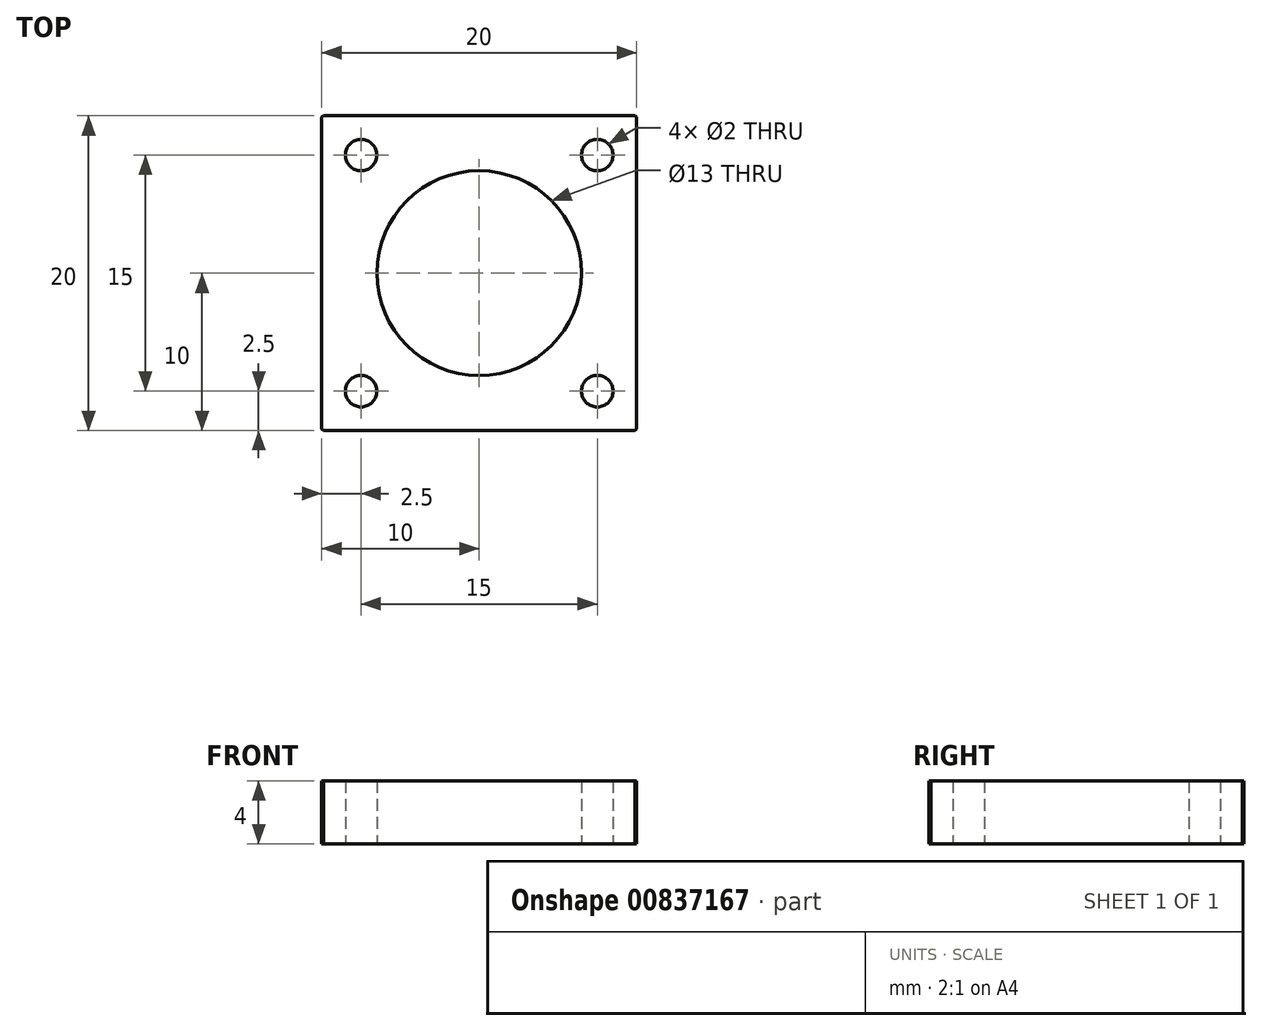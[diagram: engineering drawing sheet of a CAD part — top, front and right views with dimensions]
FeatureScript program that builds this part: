
annotation { "Feature Type Name" : "Feature", "Feature Type Description" : "" }
export const myFeature = defineFeature(function(context is Context, id is Id, definition is map)
    precondition{}
    {
        {
            var Q0;
            Q0=qCreatedBy(makeId("Top.planeOp"),FACE);
            var sketch = newSketch(context, id + "F0", { "sketchPlane" : qUnion([Q0])});
            skLineSegment(sketch, "E0.bottom", {"start": v(0, 0) * mm, "end": v(20, 0) * mm});
            skLineSegment(sketch, "E0.top", {"start": v(0, -20) * mm, "end": v(20, -20) * mm});
            skLineSegment(sketch, "E0.left", {"start": v(0, 0) * mm, "end": v(0, -20) * mm});
            skLineSegment(sketch, "E0.right", {"start": v(20, 0) * mm, "end": v(20, -20) * mm});
            skLineSegment(sketch, "E1", {"start": v(0, -10) * mm, "end": v(20, -10) * mm, "construction": true});
            skCircle(sketch, "E2", {"center": v(10, -10) * mm, "radius": 2 * mm});
            skCircle(sketch, "E3", {"center": v(10, -10) * mm, "radius": 5.5 * mm, "construction": true});
            skCircle(sketch, "E4", {"center": v(10, -10) * mm, "radius": 6.5 * mm});
            skCircle(sketch, "E5", {"center": v(10, -10) * mm, "radius": 7 * mm});
            skCircle(sketch, "E6", {"center": v(10, -10) * mm, "radius": 8.5 * mm});
            skCircle(sketch, "E7", {"center": v(10, -10) * mm, "radius": 3 * mm});
            skLineSegment(sketch, "E8", {"start": v(10, -10) * mm, "end": v(10, -5.75) * mm, "construction": true});
            skCircle(sketch, "E9", {"center": v(10, -5.75) * mm, "radius": 1.25 * mm});
            skCircle(sketch, "E10.1.0", {"center": v(5.75, -10) * mm, "radius": 1.25 * mm});
            skCircle(sketch, "E10.2.0", {"center": v(10, -14.25) * mm, "radius": 1.25 * mm});
            skCircle(sketch, "E10.3.0", {"center": v(14.25, -10) * mm, "radius": 1.25 * mm});
            skLineSegment(sketch, "E11", {"start": v(0, -2.5) * mm, "end": v(2.5, -2.5) * mm, "construction": true});
            skLineSegment(sketch, "E12", {"start": v(2.5, -2.5) * mm, "end": v(2.5, 0) * mm, "construction": true});
            skCircle(sketch, "E13", {"center": v(2.5, -2.5) * mm, "radius": 1 * mm});
            skCircle(sketch, "E14.1.0", {"center": v(2.5, -17.5) * mm, "radius": 1 * mm});
            skCircle(sketch, "E14.2.0", {"center": v(17.5, -17.5) * mm, "radius": 1 * mm});
            skCircle(sketch, "E14.3.0", {"center": v(17.5, -2.5) * mm, "radius": 1 * mm});
            skSolve(sketch);
        }
        {
            var Q0;
            Q0=makeQuery(id+"F0.imprint","IMPRINT",FACE,{"disambiguationData":[TD([[makeQuery(id+"F0.imprint","IMPRINT",EDGE,{"derivedFrom":sQuery(id+"F0.wireOp",EDGE,"E0.bottom")}),-1.0]])]});
            var Q1;
            Q1=makeQuery(id+"F0.imprint","IMPRINT",FACE,{"disambiguationData":[TD([[makeQuery(id+"F0.imprint","IMPRINT",EDGE,{"derivedFrom":sQuery(id+"F0.wireOp",EDGE,"E5")}),-1.0]])]});
            var Q2;
            Q2=makeQuery(id+"F0.imprint","IMPRINT",FACE,{"disambiguationData":[TD([[makeQuery(id+"F0.imprint","IMPRINT",EDGE,{"derivedFrom":sQuery(id+"F0.wireOp",EDGE,"E4")}),-1.0]])]});
            extrude(context, id + "F1", {"entities" : qUnion([Q0, Q1, Q2]), "depth" : 4 * mm, "offsetDistance" : 25 * mm});
        }
        {
            var Q0;
            Q0=makeQuery(id+"F1.opExtrude","SWEPT_EDGE",EDGE,{"disambiguationData":[OSD([sQuery(id+"F0.wireOp",EDGE,"E0.top"),sQuery(id+"F0.wireOp",EDGE,"E0.left")])]});
            var Q1;
            Q1=makeQuery(id+"F1.opExtrude","SWEPT_EDGE",EDGE,{"disambiguationData":[OSD([sQuery(id+"F0.wireOp",EDGE,"E0.bottom"),sQuery(id+"F0.wireOp",EDGE,"E0.left")])]});
            var Q2;
            Q2=makeQuery(id+"F1.opExtrude","SWEPT_EDGE",EDGE,{"disambiguationData":[OSD([sQuery(id+"F0.wireOp",EDGE,"E0.bottom"),sQuery(id+"F0.wireOp",EDGE,"E0.right")])]});
            var Q3;
            Q3=makeQuery(id+"F1.opExtrude","SWEPT_EDGE",EDGE,{"disambiguationData":[OSD([sQuery(id+"F0.wireOp",EDGE,"E0.top"),sQuery(id+"F0.wireOp",EDGE,"E0.right")])]});
            chamfer(context, id + "F2", {"entities" : qUnion([Q0, Q1, Q2, Q3]), "width" : .1 * mm, "tangentPropagation" : true});
        }
    });
